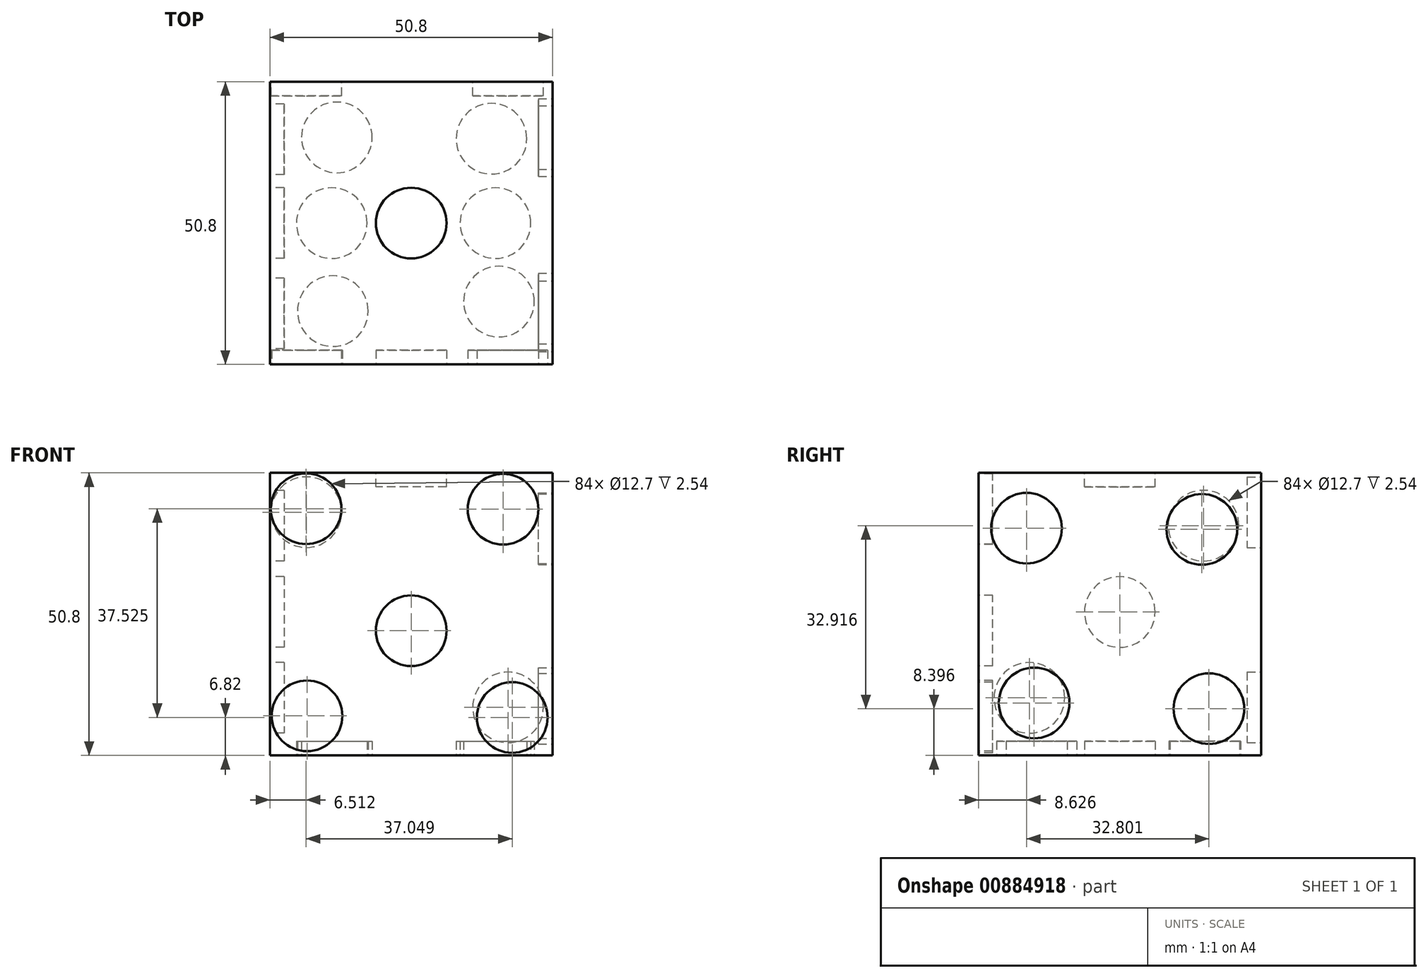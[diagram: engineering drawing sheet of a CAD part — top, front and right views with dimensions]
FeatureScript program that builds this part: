
annotation { "Feature Type Name" : "Feature", "Feature Type Description" : "" }
export const myFeature = defineFeature(function(context is Context, id is Id, definition is map)
    precondition{}
    {
        {
            var Q0;
            Q0=qCreatedBy(makeId("Top.planeOp"),FACE);
            var sketch = newSketch(context, id + "F0", { "sketchPlane" : qUnion([Q0])});
            skLineSegment(sketch, "E0.bottom", {"start": v(-25.4, 25.4) * mm, "end": v(25.4, 25.4) * mm});
            skLineSegment(sketch, "E0.top", {"start": v(-25.4, -25.4) * mm, "end": v(25.4, -25.4) * mm});
            skLineSegment(sketch, "E0.left", {"start": v(-25.4, 25.4) * mm, "end": v(-25.4, -25.4) * mm});
            skLineSegment(sketch, "E0.right", {"start": v(25.4, 25.4) * mm, "end": v(25.4, -25.4) * mm});
            skLineSegment(sketch, "E1", {"start": v(0, 25.4) * mm, "end": v(0, -25.4) * mm});
            skPoint(sketch, "E1.endSnap0", {"position": v(0, -25.4) * mm});
            skSolve(sketch);
        }
        {
            var Q0;
            Q0=makeQuery(id+"F0.imprint","IMPRINT",FACE,{"disambiguationData":[TD([[makeQuery(id+"F0.imprint","IMPRINT",EDGE,{"derivedFrom":sQuery(id+"F0.wireOp",EDGE,"E0.bottom")}),-1.0]])]});
            extrude(context, id + "F1", {"entities" : qUnion([Q0]), "depth" : 50.8 * mm, "offsetDistance" : 25.4 * mm});
        }
        {
            var Q0;
            Q0=makeQuery(id+"F1.opExtrude","CAP_FACE",FACE,{"disambiguationData":[OSD([sQuery(id+"F0.wireOp",EDGE,"E0.bottom"),sQuery(id+"F0.wireOp",EDGE,"E0.top"),sQuery(id+"F0.wireOp",EDGE,"E0.left"),sQuery(id+"F0.wireOp",EDGE,"E0.right")])],"isStart":false});
            var sketch = newSketch(context, id + "F2", { "sketchPlane" : qUnion([Q0])});
            skCircle(sketch, "E2", {"center": v(0, 0) * mm, "radius": 6.35 * mm});
            skSolve(sketch);
        }
        {
            var Q0;
            Q0=makeQuery(id+"F2.imprint","IMPRINT",FACE,{"disambiguationData":[TD([[makeQuery(id+"F2.imprint","IMPRINT",EDGE,{"derivedFrom":sQuery(id+"F2.wireOp",EDGE,"E2")}),1.0]])]});
            extrude(context, id + "F3", {"entities" : qUnion([Q0]), "operationType" : NewBodyOperationType.REMOVE, "oppositeDirection" : true, "depth" : 2.54 * mm, "offsetDistance" : 25.4 * mm});
        }
        {
            var Q0;
            Q0=makeQuery(id+"F1.opExtrude","CAP_FACE",FACE,{"disambiguationData":[OSD([sQuery(id+"F0.wireOp",EDGE,"E0.bottom"),sQuery(id+"F0.wireOp",EDGE,"E0.top"),sQuery(id+"F0.wireOp",EDGE,"E0.left"),sQuery(id+"F0.wireOp",EDGE,"E0.right")])],"isStart":true});
            var sketch = newSketch(context, id + "F4", { "sketchPlane" : qUnion([Q0])});
            skCircle(sketch, "E3", {"center": v(14.44, -15.16) * mm, "radius": 6.35 * mm});
            skCircle(sketch, "E4", {"center": v(-13.36, -15.4) * mm, "radius": 6.35 * mm});
            skCircle(sketch, "E5", {"center": v(15.16, 0) * mm, "radius": 6.35 * mm});
            skCircle(sketch, "E6", {"center": v(-14.27, 0) * mm, "radius": 6.35 * mm});
            skCircle(sketch, "E7", {"center": v(15.78, 14.12) * mm, "radius": 6.35 * mm});
            skCircle(sketch, "E8", {"center": v(-14.08, 15.83) * mm, "radius": 6.35 * mm});
            skSolve(sketch);
        }
        {
            var Q0;
            Q0=makeQuery(id+"F4.imprint","IMPRINT",FACE,{"disambiguationData":[TD([[makeQuery(id+"F4.imprint","IMPRINT",EDGE,{"derivedFrom":sQuery(id+"F4.wireOp",EDGE,"E7")}),1.0]])]});
            var Q1;
            Q1=makeQuery(id+"F4.imprint","IMPRINT",FACE,{"disambiguationData":[TD([[makeQuery(id+"F4.imprint","IMPRINT",EDGE,{"derivedFrom":sQuery(id+"F4.wireOp",EDGE,"E8")}),1.0]])]});
            var Q2;
            Q2=makeQuery(id+"F4.imprint","IMPRINT",FACE,{"disambiguationData":[TD([[makeQuery(id+"F4.imprint","IMPRINT",EDGE,{"derivedFrom":sQuery(id+"F4.wireOp",EDGE,"E5")}),1.0]])]});
            var Q3;
            Q3=makeQuery(id+"F4.imprint","IMPRINT",FACE,{"disambiguationData":[TD([[makeQuery(id+"F4.imprint","IMPRINT",EDGE,{"derivedFrom":sQuery(id+"F4.wireOp",EDGE,"E6")}),1.0]])]});
            var Q4;
            Q4=makeQuery(id+"F4.imprint","IMPRINT",FACE,{"disambiguationData":[TD([[makeQuery(id+"F4.imprint","IMPRINT",EDGE,{"derivedFrom":sQuery(id+"F4.wireOp",EDGE,"E4")}),1.0]])]});
            var Q5;
            Q5=makeQuery(id+"F4.imprint","IMPRINT",FACE,{"disambiguationData":[TD([[makeQuery(id+"F4.imprint","IMPRINT",EDGE,{"derivedFrom":sQuery(id+"F4.wireOp",EDGE,"E3")}),1.0]])]});
            extrude(context, id + "F5", {"entities" : qUnion([Q0, Q1, Q2, Q3, Q4, Q5]), "operationType" : NewBodyOperationType.REMOVE, "oppositeDirection" : true, "depth" : 2.54 * mm, "offsetDistance" : 25.4 * mm});
        }
        {
            var Q0;
            Q0=makeQuery(id+"F1.opExtrude","SWEPT_FACE",FACE,{"disambiguationData":[OSD([sQuery(id+"F0.wireOp",EDGE,"E0.top")])]});
            var sketch = newSketch(context, id + "F6", { "sketchPlane" : qUnion([Q0])});
            skCircle(sketch, "E9", {"center": v(18.16, 6.82) * mm, "radius": 6.35 * mm});
            skCircle(sketch, "E10", {"center": v(-18.72, 7.1) * mm, "radius": 6.35 * mm});
            skCircle(sketch, "E11", {"center": v(0, 22.4) * mm, "radius": 6.35 * mm});
            skCircle(sketch, "E12", {"center": v(16.53, 44.24) * mm, "radius": 6.35 * mm});
            skCircle(sketch, "E13", {"center": v(-18.89, 44.35) * mm, "radius": 6.35 * mm});
            skSolve(sketch);
        }
        {
            var Q0;
            Q0=makeQuery(id+"F6.imprint","IMPRINT",FACE,{"disambiguationData":[TD([[makeQuery(id+"F6.imprint","IMPRINT",EDGE,{"derivedFrom":sQuery(id+"F6.wireOp",EDGE,"E9")}),1.0]])]});
            var Q1;
            Q1=makeQuery(id+"F6.imprint","IMPRINT",FACE,{"disambiguationData":[TD([[makeQuery(id+"F6.imprint","IMPRINT",EDGE,{"derivedFrom":sQuery(id+"F6.wireOp",EDGE,"E10")}),1.0]])]});
            var Q2;
            Q2=makeQuery(id+"F6.imprint","IMPRINT",FACE,{"disambiguationData":[TD([[makeQuery(id+"F6.imprint","IMPRINT",EDGE,{"derivedFrom":sQuery(id+"F6.wireOp",EDGE,"E11")}),1.0]])]});
            var Q3;
            Q3=makeQuery(id+"F6.imprint","IMPRINT",FACE,{"disambiguationData":[TD([[makeQuery(id+"F6.imprint","IMPRINT",EDGE,{"derivedFrom":sQuery(id+"F6.wireOp",EDGE,"E12")}),1.0]])]});
            var Q4;
            Q4=makeQuery(id+"F6.imprint","IMPRINT",FACE,{"disambiguationData":[TD([[makeQuery(id+"F6.imprint","IMPRINT",EDGE,{"derivedFrom":sQuery(id+"F6.wireOp",EDGE,"E13")}),1.0]])]});
            extrude(context, id + "F7", {"entities" : qUnion([Q0, Q1, Q2, Q3, Q4]), "operationType" : NewBodyOperationType.REMOVE, "oppositeDirection" : true, "depth" : 2.54 * mm, "offsetDistance" : 25.4 * mm});
        }
        {
            var Q0;
            Q0=makeQuery(id+"F1.opExtrude","SWEPT_FACE",FACE,{"disambiguationData":[OSD([sQuery(id+"F0.wireOp",EDGE,"E0.right")])]});
            var sketch = newSketch(context, id + "F8", { "sketchPlane" : qUnion([Q0])});
            skCircle(sketch, "E14", {"center": v(-16.77, 40.85) * mm, "radius": 6.35 * mm});
            skCircle(sketch, "E15", {"center": v(14.76, 40.62) * mm, "radius": 6.35 * mm});
            skCircle(sketch, "E16", {"center": v(-15.4, 9.43) * mm, "radius": 6.35 * mm});
            skCircle(sketch, "E17", {"center": v(16.03, 8.4) * mm, "radius": 6.35 * mm});
            skSolve(sketch);
        }
        {
            var Q0;
            Q0=makeQuery(id+"F8.imprint","IMPRINT",FACE,{"disambiguationData":[TD([[makeQuery(id+"F8.imprint","IMPRINT",EDGE,{"derivedFrom":sQuery(id+"F8.wireOp",EDGE,"E14")}),1.0]])]});
            var Q1;
            Q1=makeQuery(id+"F8.imprint","IMPRINT",FACE,{"disambiguationData":[TD([[makeQuery(id+"F8.imprint","IMPRINT",EDGE,{"derivedFrom":sQuery(id+"F8.wireOp",EDGE,"E15")}),1.0]])]});
            var Q2;
            Q2=makeQuery(id+"F8.imprint","IMPRINT",FACE,{"disambiguationData":[TD([[makeQuery(id+"F8.imprint","IMPRINT",EDGE,{"derivedFrom":sQuery(id+"F8.wireOp",EDGE,"E16")}),1.0]])]});
            var Q3;
            Q3=makeQuery(id+"F8.imprint","IMPRINT",FACE,{"disambiguationData":[TD([[makeQuery(id+"F8.imprint","IMPRINT",EDGE,{"derivedFrom":sQuery(id+"F8.wireOp",EDGE,"E17")}),1.0]])]});
            extrude(context, id + "F9", {"entities" : qUnion([Q0, Q1, Q2, Q3]), "operationType" : NewBodyOperationType.REMOVE, "oppositeDirection" : true, "depth" : 2.54 * mm, "offsetDistance" : 25.4 * mm});
        }
        {
            var Q0;
            Q0=makeQuery(id+"F1.opExtrude","SWEPT_FACE",FACE,{"disambiguationData":[OSD([sQuery(id+"F0.wireOp",EDGE,"E0.left")])]});
            var sketch = newSketch(context, id + "F10", { "sketchPlane" : qUnion([Q0])});
            skCircle(sketch, "E18", {"center": v(0, 25.77) * mm, "radius": 6.35 * mm});
            skCircle(sketch, "E19", {"center": v(-15.05, 41.31) * mm, "radius": 6.35 * mm});
            skCircle(sketch, "E20", {"center": v(16.26, 10.35) * mm, "radius": 6.35 * mm});
            skSolve(sketch);
        }
        {
            var Q0;
            Q0=makeQuery(id+"F10.imprint","IMPRINT",FACE,{"disambiguationData":[TD([[makeQuery(id+"F10.imprint","IMPRINT",EDGE,{"derivedFrom":sQuery(id+"F10.wireOp",EDGE,"E18")}),1.0]])]});
            var Q1;
            Q1=makeQuery(id+"F10.imprint","IMPRINT",FACE,{"disambiguationData":[TD([[makeQuery(id+"F10.imprint","IMPRINT",EDGE,{"derivedFrom":sQuery(id+"F10.wireOp",EDGE,"E20")}),1.0]])]});
            var Q2;
            Q2=makeQuery(id+"F10.imprint","IMPRINT",FACE,{"disambiguationData":[TD([[makeQuery(id+"F10.imprint","IMPRINT",EDGE,{"derivedFrom":sQuery(id+"F10.wireOp",EDGE,"E19")}),1.0]])]});
            extrude(context, id + "F11", {"entities" : qUnion([Q0, Q1, Q2]), "operationType" : NewBodyOperationType.REMOVE, "oppositeDirection" : true, "depth" : 2.54 * mm, "offsetDistance" : 25.4 * mm});
        }
        {
            var Q0;
            Q0=makeQuery(id+"F1.opExtrude","SWEPT_FACE",FACE,{"disambiguationData":[OSD([sQuery(id+"F0.wireOp",EDGE,"E0.bottom")])]});
            var sketch = newSketch(context, id + "F12", { "sketchPlane" : qUnion([Q0])});
            skCircle(sketch, "E21", {"center": v(-17.4, 8.63) * mm, "radius": 6.35 * mm});
            skCircle(sketch, "E22", {"center": v(18.85, 43.73) * mm, "radius": 6.35 * mm});
            skSolve(sketch);
        }
        {
            var Q0;
            Q0 = qSketchRegion(id + "F12", true);
            extrude(context, id + "F13", {"entities" : qUnion([Q0]), "operationType" : NewBodyOperationType.REMOVE, "oppositeDirection" : true, "depth" : 2.54 * mm, "offsetDistance" : 25.4 * mm});
        }
    });
